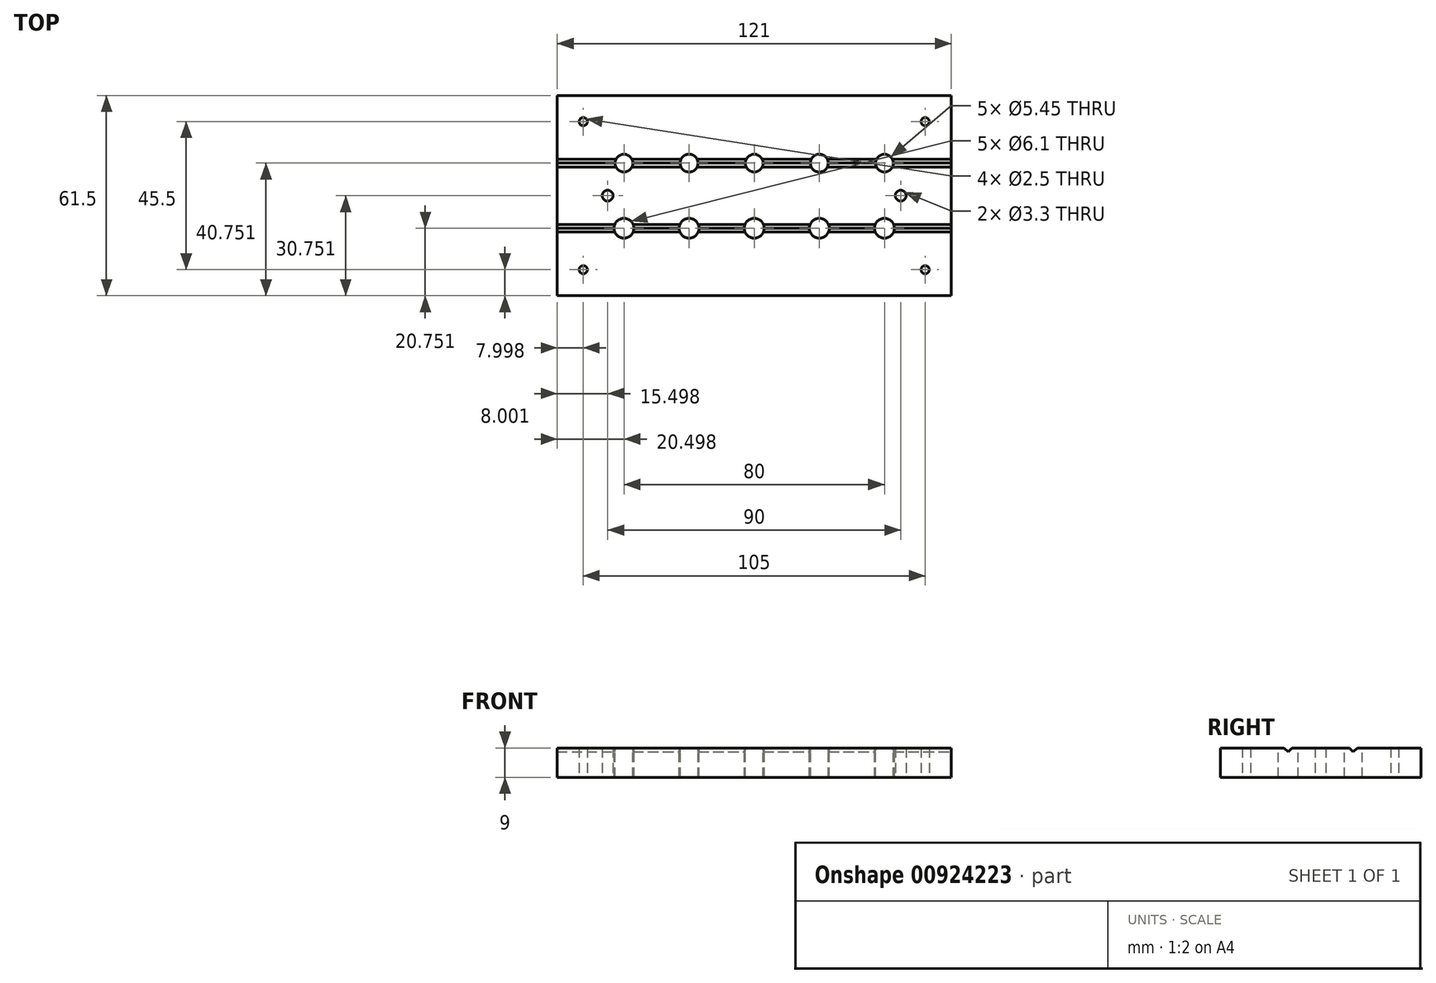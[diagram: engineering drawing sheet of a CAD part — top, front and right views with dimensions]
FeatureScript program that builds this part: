
annotation { "Feature Type Name" : "Feature", "Feature Type Description" : "" }
export const myFeature = defineFeature(function(context is Context, id is Id, definition is map)
    precondition{}
    {
        {
            var Q0;
            Q0=qCreatedBy(makeId("Top.planeOp"),FACE);
            var sketch = newSketch(context, id + "F0", { "sketchPlane" : qUnion([Q0])});
            skLineSegment(sketch, "E0.bottom", {"start": v(-105.25, 36.33) * mm, "end": v(15.75, 36.33) * mm});
            skLineSegment(sketch, "E0.top", {"start": v(-105.25, -25.17) * mm, "end": v(15.75, -25.17) * mm});
            skLineSegment(sketch, "E0.left", {"start": v(-105.25, 36.33) * mm, "end": v(-105.25, -25.17) * mm});
            skLineSegment(sketch, "E0.right", {"start": v(15.75, 36.33) * mm, "end": v(15.75, -25.17) * mm});
            skSolve(sketch);
        }
        {
            var Q0;
            Q0 = qSketchRegion(id + "F0", true);
            extrude(context, id + "F1", {"entities" : qUnion([Q0]), "oppositeDirection" : true, "depth" : 9 * mm, "offsetDistance" : 25 * mm});
        }
        {
            var Q0;
            Q0=makeQuery(id+"F1.opExtrude","CAP_FACE",FACE,{"disambiguationData":[OSD([sQuery(id+"F0.wireOp",EDGE,"E0.bottom"),sQuery(id+"F0.wireOp",EDGE,"E0.top"),sQuery(id+"F0.wireOp",EDGE,"E0.left"),sQuery(id+"F0.wireOp",EDGE,"E0.right")])],"isStart":true});
            var sketch = newSketch(context, id + "F2", { "sketchPlane" : qUnion([Q0])});
            skCircle(sketch, "E1", {"center": v(-84.75, 15.58) * mm, "radius": 2.73 * mm});
            skCircle(sketch, "E2", {"center": v(-84.75, -4.42) * mm, "radius": 3.05 * mm});
            skCircle(sketch, "E3", {"center": v(-64.75, 15.58) * mm, "radius": 2.73 * mm});
            skCircle(sketch, "E4", {"center": v(-64.75, -4.42) * mm, "radius": 3.05 * mm});
            skCircle(sketch, "E5", {"center": v(-44.75, 15.58) * mm, "radius": 2.73 * mm});
            skCircle(sketch, "E6", {"center": v(-44.75, -4.42) * mm, "radius": 3.05 * mm});
            skCircle(sketch, "E7", {"center": v(-24.75, 15.58) * mm, "radius": 2.73 * mm});
            skCircle(sketch, "E8", {"center": v(-24.75, -4.42) * mm, "radius": 3.05 * mm});
            skCircle(sketch, "E9", {"center": v(-4.75, 15.58) * mm, "radius": 2.73 * mm});
            skCircle(sketch, "E10", {"center": v(-4.75, -4.42) * mm, "radius": 3.05 * mm});
            skSolve(sketch);
        }
        {
            var Q0;
            Q0 = qSketchRegion(id + "F2", true);
            extrude(context, id + "F3", {"entities" : qUnion([Q0]), "operationType" : NewBodyOperationType.REMOVE, "oppositeDirection" : true, "depth" : 10 * mm, "offsetDistance" : 25 * mm});
        }
        {
            var Q0;
            Q0=makeQuery(id+"F1.opExtrude","CAP_FACE",FACE,{"disambiguationData":[OSD([sQuery(id+"F0.wireOp",EDGE,"E0.bottom"),sQuery(id+"F0.wireOp",EDGE,"E0.top"),sQuery(id+"F0.wireOp",EDGE,"E0.left"),sQuery(id+"F0.wireOp",EDGE,"E0.right")])],"isStart":false});
            var sketch = newSketch(context, id + "F4", { "sketchPlane" : qUnion([Q0])});
            skCircle(sketch, "E11", {"center": v(-97.25, 17.17) * mm, "radius": 1.25 * mm});
            skCircle(sketch, "E12", {"center": v(-97.25, -28.33) * mm, "radius": 1.25 * mm});
            skCircle(sketch, "E13", {"center": v(7.75, 17.17) * mm, "radius": 1.25 * mm});
            skCircle(sketch, "E14", {"center": v(7.75, -28.33) * mm, "radius": 1.25 * mm});
            skSolve(sketch);
        }
        {
            var Q0;
            Q0 = qSketchRegion(id + "F4", true);
            extrude(context, id + "F5", {"entities" : qUnion([Q0]), "operationType" : NewBodyOperationType.REMOVE, "oppositeDirection" : true, "depth" : 10 * mm, "offsetDistance" : 25 * mm});
        }
        {
            var Q0;
            Q0=makeQuery(id+"F1.opExtrude","CAP_FACE",FACE,{"disambiguationData":[OSD([sQuery(id+"F0.wireOp",EDGE,"E0.bottom"),sQuery(id+"F0.wireOp",EDGE,"E0.top"),sQuery(id+"F0.wireOp",EDGE,"E0.left"),sQuery(id+"F0.wireOp",EDGE,"E0.right")])],"isStart":false});
            var sketch = newSketch(context, id + "F6", { "sketchPlane" : qUnion([Q0])});
            skCircle(sketch, "E15", {"center": v(-89.75, -5.58) * mm, "radius": 1.65 * mm});
            skCircle(sketch, "E16", {"center": v(0.25, -5.58) * mm, "radius": 1.65 * mm});
            skSolve(sketch);
        }
        {
            var Q0;
            Q0 = qSketchRegion(id + "F6", true);
            extrude(context, id + "F7", {"entities" : qUnion([Q0]), "operationType" : NewBodyOperationType.REMOVE, "oppositeDirection" : true, "depth" : 10 * mm, "offsetDistance" : 25 * mm});
        }
        {
            var Q0;
            Q0=makeQuery(id+"F1.opExtrude","SWEPT_FACE",FACE,{"disambiguationData":[OSD([sQuery(id+"F0.wireOp",EDGE,"E0.right")])]});
            var sketch = newSketch(context, id + "F8", { "sketchPlane" : qUnion([Q0])});
            skLineSegment(sketch, "E17", {"start": v(-5.62, 0) * mm, "end": v(-3.22, 0) * mm});
            skLineSegment(sketch, "E18", {"start": v(-3.22, 0) * mm, "end": v(-4.42, -1.2) * mm});
            skLineSegment(sketch, "E19", {"start": v(-4.42, -1.2) * mm, "end": v(-5.62, 0) * mm});
            skLineSegment(sketch, "E20", {"start": v(14.38, 0) * mm, "end": v(16.78, 0) * mm});
            skLineSegment(sketch, "E21", {"start": v(16.78, 0) * mm, "end": v(15.58, -1.2) * mm});
            skLineSegment(sketch, "E22", {"start": v(15.58, -1.2) * mm, "end": v(14.38, 0) * mm});
            skSolve(sketch);
        }
        {
            var Q0;
            Q0 = qSketchRegion(id + "F8", true);
            extrude(context, id + "F9", {"entities" : qUnion([Q0]), "operationType" : NewBodyOperationType.REMOVE, "oppositeDirection" : true, "depth" : 125 * mm, "offsetDistance" : 25 * mm});
        }
    });
